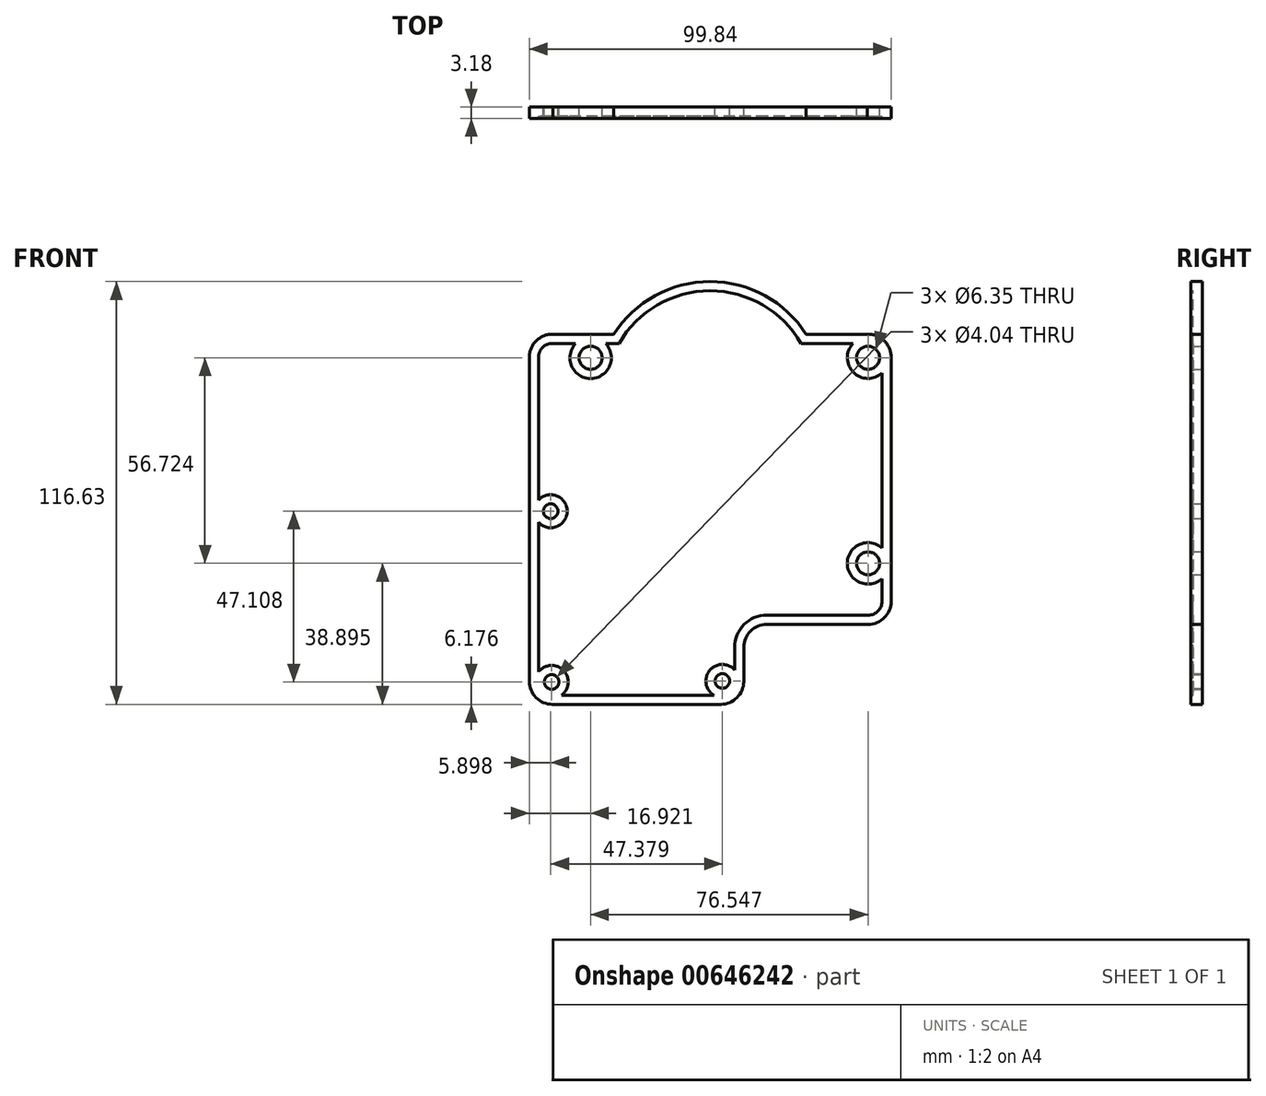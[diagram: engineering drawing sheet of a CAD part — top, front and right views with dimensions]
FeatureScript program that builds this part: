
annotation { "Feature Type Name" : "Feature", "Feature Type Description" : "" }
export const myFeature = defineFeature(function(context is Context, id is Id, definition is map)
    precondition{}
    {
        {
            var Q0;
            Q0=qCreatedBy(makeId("Front.planeOp"),FACE);
            var sketch = newSketch(context, id + "F0", { "sketchPlane" : qUnion([Q0])});
            skLineSegment(sketch, "E0", {"start": v(56.73, 41.26) * mm, "end": v(56.73, -26.07) * mm});
            skLineSegment(sketch, "E1", {"start": v(50.38, -32.42) * mm, "end": v(22.42, -32.42) * mm});
            skLineSegment(sketch, "E2", {"start": v(16.07, -38.77) * mm, "end": v(16.07, -48.14) * mm});
            skLineSegment(sketch, "E3", {"start": v(9.72, -54.49) * mm, "end": v(-36.76, -54.49) * mm});
            skLineSegment(sketch, "E4", {"start": v(-43.11, -48.14) * mm, "end": v(-43.11, 41.26) * mm});
            skPoint(sketch, "E5.center", {"position": v(-43.11, 47.74) * mm});
            skPoint(sketch, "E6.2.0", {"position": v(-124.7, 54.47) * mm});
            skCircle(sketch, "E7", {"center": v(-37.21, -1.2) * mm, "radius": 2.02 * mm});
            skCircle(sketch, "E8.1.0", {"center": v(-36.94, -48.31) * mm, "radius": 2.02 * mm});
            skCircle(sketch, "E8.2.0", {"center": v(10.17, -48.04) * mm, "radius": 2.02 * mm});
            skPoint(sketch, "E8.center", {"position": v(-13.52, -24.62) * mm});
            skCircle(sketch, "E9", {"center": v(50.36, -15.6) * mm, "radius": 3.18 * mm});
            skCircle(sketch, "E10", {"center": v(50.36, 41.13) * mm, "radius": 3.18 * mm});
            skCircle(sketch, "E11", {"center": v(-26.19, 41.13) * mm, "radius": 3.18 * mm});
            skPoint(sketch, "E12.visualSharp", {"position": v(56.73, 47.74) * mm});
            skArc(sketch, "E12.filletArc", {"start": v(56.73, 41.26) * mm, "mid": v(54.8, 45.83) * mm, "end": v(50.17, 47.6) * mm});
            skPoint(sketch, "E13.visualSharp", {"position": v(56.73, -32.42) * mm});
            skArc(sketch, "E13.filletArc", {"start": v(50.38, -32.42) * mm, "mid": v(54.87, -30.56) * mm, "end": v(56.73, -26.07) * mm});
            skPoint(sketch, "E14.visualSharp", {"position": v(16.07, -54.49) * mm});
            skArc(sketch, "E14.filletArc", {"start": v(9.72, -54.49) * mm, "mid": v(14.2, -52.63) * mm, "end": v(16.07, -48.14) * mm});
            skPoint(sketch, "E15.visualSharp", {"position": v(-43.11, -54.49) * mm});
            skArc(sketch, "E15.filletArc", {"start": v(-43.11, -48.14) * mm, "mid": v(-41.25, -52.63) * mm, "end": v(-36.76, -54.49) * mm});
            skArc(sketch, "E16.filletArc", {"start": v(-36.55, 47.6) * mm, "mid": v(-41.18, 45.83) * mm, "end": v(-43.11, 41.26) * mm});
            skLineSegment(sketch, "E17", {"start": v(-36.55, 47.6) * mm, "end": v(-19.78, 47.6) * mm});
            skLineSegment(sketch, "E18", {"start": v(50.17, 47.6) * mm, "end": v(33.3, 47.6) * mm});
            skArc(sketch, "E19", {"start": v(33.3, 47.6) * mm, "mid": v(6.76, 62.14) * mm, "end": v(-19.78, 47.6) * mm});
            skPoint(sketch, "E20.visualSharp", {"position": v(16.07, -32.42) * mm});
            skArc(sketch, "E20.filletArc", {"start": v(22.42, -32.42) * mm, "mid": v(17.93, -34.28) * mm, "end": v(16.07, -38.77) * mm});
            skSolve(sketch);
        }
        {
            var Q0;
            Q0=makeQuery(id+"F0.imprint","IMPRINT",FACE,{"disambiguationData":[TD([[makeQuery(id+"F0.imprint","IMPRINT",EDGE,{"derivedFrom":sQuery(id+"F0.wireOp",EDGE,"E0")}),-1.0]])]});
            extrude(context, id + "F1", {"entities" : qUnion([Q0]), "depth" : 3.17 * mm, "offsetDistance" : 25.4 * mm});
        }
        {
            var Q0;
            Q0=makeQuery(id+"F1.opExtrude","CAP_FACE",FACE,{"disambiguationData":[OSD([sQuery(id+"F0.wireOp",EDGE,"E0"),sQuery(id+"F0.wireOp",EDGE,"E1"),sQuery(id+"F0.wireOp",EDGE,"E2"),sQuery(id+"F0.wireOp",EDGE,"E3"),sQuery(id+"F0.wireOp",EDGE,"E4"),sQuery(id+"F0.wireOp",EDGE,"E7"),sQuery(id+"F0.wireOp",EDGE,"E8.1.0"),sQuery(id+"F0.wireOp",EDGE,"E8.2.0"),sQuery(id+"F0.wireOp",EDGE,"E9"),sQuery(id+"F0.wireOp",EDGE,"E10"),sQuery(id+"F0.wireOp",EDGE,"E11"),sQuery(id+"F0.wireOp",EDGE,"E12.filletArc"),sQuery(id+"F0.wireOp",EDGE,"E13.filletArc"),sQuery(id+"F0.wireOp",EDGE,"E14.filletArc"),sQuery(id+"F0.wireOp",EDGE,"E15.filletArc"),sQuery(id+"F0.wireOp",EDGE,"E16.filletArc"),sQuery(id+"F0.wireOp",EDGE,"E17"),sQuery(id+"F0.wireOp",EDGE,"E18"),sQuery(id+"F0.wireOp",EDGE,"E19"),sQuery(id+"F0.wireOp",EDGE,"E20.filletArc")])],"isStart":false});
            shell(context, id + "F2", {"entities" : qUnion([Q0]), "thickness" : 2.54 * mm});
        }
    });
